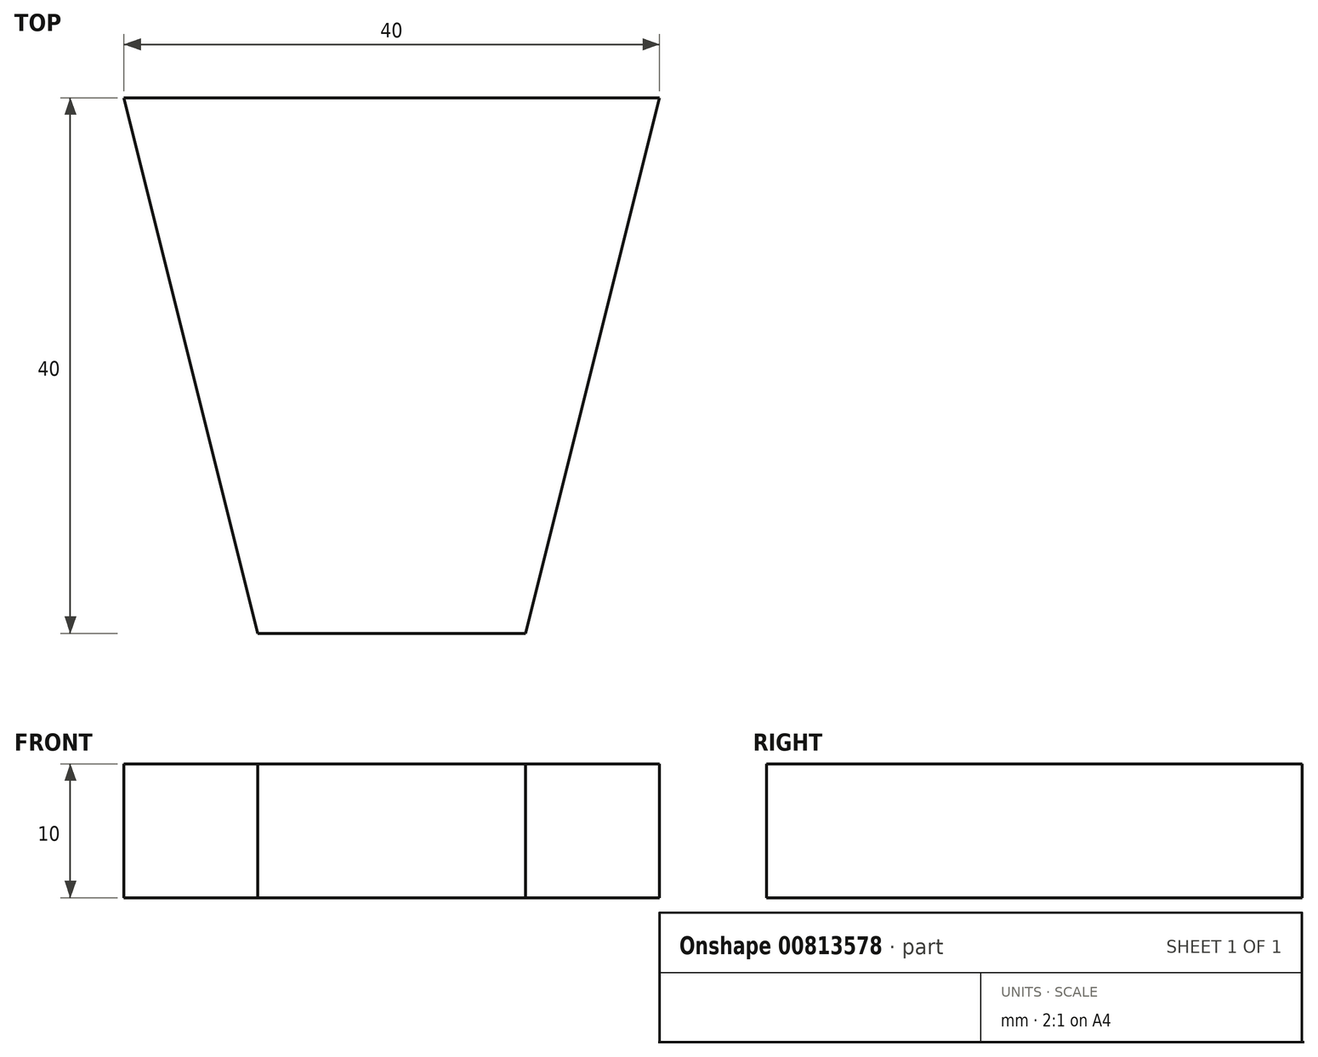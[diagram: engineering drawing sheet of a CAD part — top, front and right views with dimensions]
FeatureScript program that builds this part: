
annotation { "Feature Type Name" : "Feature", "Feature Type Description" : "" }
export const myFeature = defineFeature(function(context is Context, id is Id, definition is map)
    precondition{}
    {
        {
            var Q0;
            Q0=qCreatedBy(makeId("Top.planeOp"),FACE);
            var sketch = newSketch(context, id + "F0", { "sketchPlane" : qUnion([Q0])});
            skLineSegment(sketch, "E0", {"start": v(-30, 20) * mm, "end": v(10, 20) * mm});
            skLineSegment(sketch, "E1.MirrorCS", {"start": v(-20, -20) * mm, "end": v(0, -20) * mm});
            skLineSegment(sketch, "E2", {"start": v(-30, 20) * mm, "end": v(-20, -20) * mm});
            skLineSegment(sketch, "E3", {"start": v(10, 20) * mm, "end": v(0, -20) * mm});
            skPoint(sketch, "E4.orphan", {"position": v(-30, -20) * mm});
            skPoint(sketch, "E5.orphan", {"position": v(10, -20) * mm});
            skSolve(sketch);
        }
        {
            var Q0;
            Q0=makeQuery(id+"F0.imprint","IMPRINT",FACE,{"disambiguationData":[TD([[makeQuery(id+"F0.imprint","IMPRINT",EDGE,{"derivedFrom":sQuery(id+"F0.wireOp",EDGE,"E0")}),-1.0]])]});
            extrude(context, id + "F1", {"entities" : qUnion([Q0]), "depth" : 10 * mm, "offsetDistance" : 25 * mm});
        }
    });
